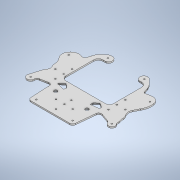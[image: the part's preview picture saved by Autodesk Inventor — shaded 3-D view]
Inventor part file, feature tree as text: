
AUTODESK INVENTOR PART (.ipt)
format: ipt  version: 2021 (Build 250183000, 183)  size: 653,824 bytes
history: native  units: mm
features: other x7, sketch x3, hole x1, extrude x1, fillet x1, projected_geometry x1
ambient origin geometry x8: Origin, YZ Plane, XZ Plane, XY Plane, X Axis, Y Axis, Z Axis, Center Point
bodies: Body1 (feature_tree)
feature tree (14):
  other  "AMR轉接板金"
  other  "AMR-純外殼.ipt"
  hole  "孔1"  [1 undecoded]
  sketch  "草圖3"
  extrude  "擠出1"  Depth=190.0mm
  fillet  "圓角1"  Radius=141.25mm
  sketch  "草圖2"
  other  "螺紋1"
  other  "實體40::AMR-純外殼.ipt"
  other  "標籤特徵1"
  sketch  "草圖1"
  projected_geometry  "投影迴路1"
  other  "實體1"
  other  "MeshFeature1"
note: 1 required parameter value undecoded (feature->parameter linkage not recoverable at this tier; creation-order binding heuristic only, values carry confidence <= 0.55)
